# Revit family: Worksurface-Teknion-PLSW__Semisupported_Worksurface-R2015
name_source: partatom
category: Furniture
revit_build: Autodesk Revit Architecture 2015 (Build: 20140323_1530(x64)
units: mm (PartAtom-declared; Revit-internal decimal feet)

## types (4) — shared parameters
Assembly Code = E2020200
Manufacturer = Teknion
Manufacturer Fax = 416.661.4586
Part Number = PLSW
Product Documentation Link = http://www.teknion.com
Product Line = Filing and Storage
Product Page URL = http://www.teknion.com
Series = Ledger Plus
Sustainability Data = http://www.teknion.com
URL = www.teknion.com
Unit Weight URL = http://www.teknion.com
Warranty = http://www.teknion.com
Worksurface Thickness = 1 "

## per-type parameters (varying)
| type | Description | District Leg Style | Loop Leg Style | Model | Only Rectangular Top | Pedestal Leg Style |
| Loop Leg Style - Rectangular Top | Semi-Supported Rectangular Top Worksurface, Loop Leg Application | No | Yes | PLSWRL_ | Yes | No |
| District Leg - Rectangular Top | Semi-Supported Rectangular Top Worksurface, District Leg Application | Yes | No | PLSWRD_ | Yes | No |
| Pedestal Leg Style - Bullet Top | Semi-Supported Bullet Top Worksurface, Pedestal Leg Application | No | No | PLSWBP_ | No | Yes |
| Pedestal Leg Style - Rectangular Top | Semi-Supported Rectangular Top Worksurface, Pedestal Application | No | No | PLSWRP_ | Yes | Yes |

## geometry (parser evidence)
native form markers: Sweep x2
no freeform markers — native parametric forms only
